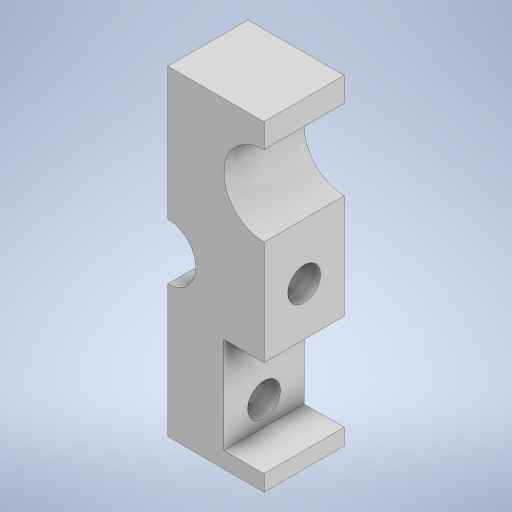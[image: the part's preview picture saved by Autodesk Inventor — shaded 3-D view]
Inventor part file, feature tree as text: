
AUTODESK INVENTOR PART (.ipt)
format: ipt  version: 2023 (Build 270158000, 158)  size: 321,024 bytes
history: native  units: mm
features: extrude x7, sketch x7, plane x1
ambient origin geometry x8: Origin, YZ Plane, XZ Plane, XY Plane, X Axis, Y Axis, Z Axis, Center Point
bodies: Solid1 (feature_tree)
feature tree (15):
  extrude  "Extrusion1"  Depth=20.0mm
  plane  "Work Plane1"
  extrude  "Extrusion2"  Depth=2.0mm
  extrude  "Extrusion3"  Depth=4.0mm
  extrude  "Extrusion4"  Depth=5.0mm TaperAngle=0.0deg
  extrude  "Extrusion5"  Depth=1.8mm TaperAngle=0.0deg
  extrude  "Extrusion6"  Depth=8.0mm TaperAngle=0.0deg
  extrude  "Extrusion7"  Depth=10.0mm
  sketch  "Sketch1"  dims[d0=20.0mm d1=20.0mm]
  sketch  "Sketch2"  dims[d2=4.0mm d6=2.0mm]
  sketch  "Sketch3"  dims[d7=2.0mm d8=4.0mm]
  sketch  "Sketch4"  dims[d9=2.0mm d10=5.0mm d11=0.0mm]
  sketch  "Sketch5"  dims[d12=5.5mm d13=1.8mm d14=0.0mm]
  sketch  "Sketch6"  dims[d15=3.5mm d16=8.0mm d17=0.0mm]
  sketch  "Sketch7"  dims[d18=2.05mm d19=2.05mm d20=2.5mm d21=2.5mm d22=2.5mm d23=2.5mm d24=5.0mm d25=0.0mm d30=5.0mm d31=0.0mm d32=2.5mm d33=1.0mm d34=6.0mm d35=5.0mm d36=4.0mm d37=5.0mm d38=0.0mm d39=2.5mm d40=10.0mm d41=2.05mm d42=20.0mm d43=0.0mm]
